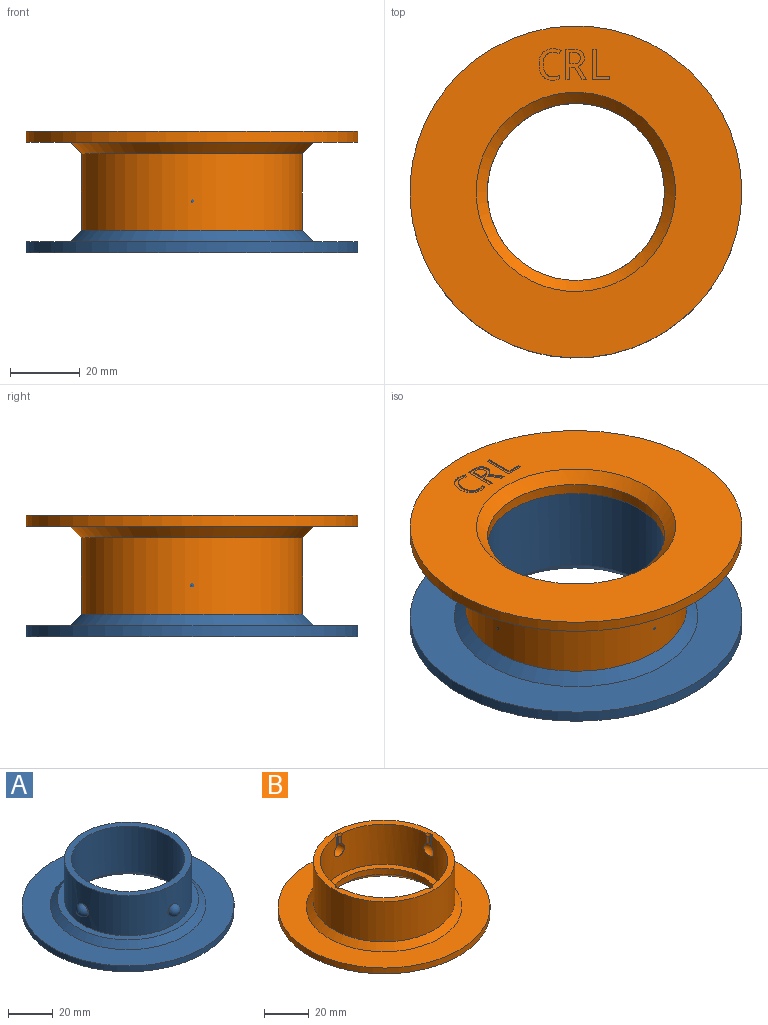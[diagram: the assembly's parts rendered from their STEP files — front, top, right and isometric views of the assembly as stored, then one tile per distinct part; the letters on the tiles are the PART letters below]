
ASSEMBLY  parts=2 mates=1
PART A: 62 faces, bbox 95.3x95.3x28.4 mm
  f0: plane 95.25x95.25mm, normal (0,0,-1), area 4479.2mm2, adj f10,f11,f27,f28,f29,f30,f31,f32
  f1: cylinder r=3.17mm len=6.35mm, axis (0,1,0), area 0.9mm2, adj f5,f20
  f2: cylinder r=3.17mm len=6.35mm, axis (0,1,0), area 0.9mm2, adj f5,f19
  f3: cylinder r=3.17mm len=6.35mm, axis (-1,0,0), area 0.9mm2, adj f5,f18
  f4: cylinder r=3.17mm len=6.35mm, axis (-1,0,0), area 0.9mm2, adj f5,f17
  f5: cylinder r=28.57mm len=57.15mm, axis (0,0,1), area 3833.8mm2, adj f1,f2,f3,f4,f8,f9,f13,f14
  f6: cylinder r=25.4mm len=50.8mm, axis (0,0,1), area 4027.3mm2, adj f9,f11
  f7: plane 95.25x95.25mm, normal (0,0,1), area 3293.6mm2, adj f10,f12
  f8: plane 63.5x63.5mm, normal (0,0,1), area 601.7mm2, adj f5,f12
  f9: plane 57.15x57.15mm, normal (0,0,1), area 538.4mm2, adj f5,f6
  f10: cylinder r=47.62mm len=95.25mm, axis (0,0,1), area 950.1mm2, adj f0,f7
  f11: cone r=28.57mm half-angle=45deg, axis (0,0,-1), area 761.4mm2, adj f0,f6
  f12: cone r=31.75mm half-angle=45deg, axis (0,0,-1), area 940.5mm2, adj f7,f8
  f13: cylinder r=3.17mm len=6.35mm, axis (0,1,0), area 0.9mm2, adj f5,f19
  f14: cylinder r=3.17mm len=6.35mm, axis (0,1,0), area 0.9mm2, adj f5,f20
  f15: cylinder r=3.17mm len=6.35mm, axis (-1,0,0), area 0.9mm2, adj f5,f17
  f16: cylinder r=3.17mm len=6.35mm, axis (-1,0,0), area 0.9mm2, adj f5,f18
  f17: sphere r=3.17mm, area 63.3mm2, adj f4,f15
  f18: sphere r=3.17mm, area 63.3mm2, adj f3,f16
  f19: sphere r=3.17mm, area 63.3mm2, adj f2,f13
  f20: sphere r=3.17mm, area 63.3mm2, adj f1,f14
  f21: plane 1.11x0.4mm, normal (0,1,0), area 0.4mm2, adj f22,f37,f38,f61
  f22: plane 3.65x0.4mm, normal (-1,0,0), area 1.4mm2, adj f21,f23,f38,f61
  f23: plane 1.07x0.4mm, normal (0,-1,0), area 0.4mm2, adj f22,f24,f38,f61
  f24: extruded ~1.74x0.42mm, area 0.7mm2, adj f23,f25,f38,f61
  f25: extruded ~1.37x0.54mm, area 0.6mm2, adj f24,f26,f38,f61
  f26: extruded ~1.42x0.55mm, area 0.6mm2, adj f25,f37,f38,f61
  f27: plane 4.08x0.4mm, normal (-1,0,0), area 1.6mm2, adj f0,f28,f36,f38
  f28: plane 1.54x0.4mm, normal (0,-1,0), area 0.6mm2, adj f0,f27,f29,f38
  f29: plane 4.08x2.36mm, normal (0.87,-0.5,0), area 1.9mm2, adj f0,f28,f30,f38
  f30: plane 1.48x0.4mm, normal (0,-1,0), area 0.6mm2, adj f0,f29,f31,f38
  f31: plane 4.42x2.68mm, normal (-0.86,0.52,0), area 2.1mm2, adj f0,f30,f32,f38
  f32: extruded ~2.65x1.95mm, area 1.4mm2, adj f0,f31,f33,f38
  f33: extruded ~3.51x2.8mm, area 2mm2, adj f0,f32,f34,f38
  f34: plane 2.41x0.4mm, normal (0,1,0), area 1mm2, adj f0,f33,f35,f38
  f35: plane 9.87x0.4mm, normal (1,0,0), area 3.9mm2, adj f0,f34,f36,f38
  f36: plane 1.26x0.4mm, normal (0,-1,0), area 0.5mm2, adj f0,f27,f35,f38
  f37: extruded ~1.7x0.45mm, area 0.7mm2, adj f21,f26,f38,f61
  f38: plane 9.87x6.65mm, normal (0,0,-1), area 30.7mm2, adj f21,f22,f23,f24,f25,f26,f27,f28
  f39: plane 9.87x0.4mm, normal (1,0,0), area 3.9mm2, adj f0,f40,f44,f45
  f40: plane 5.55x0.4mm, normal (0,-1,0), area 2.2mm2, adj f0,f39,f41,f45
  f41: plane 1.12x0.4mm, normal (-1,0,0), area 0.4mm2, adj f0,f40,f42,f45
  f42: plane 4.29x0.4mm, normal (0,1,0), area 1.7mm2, adj f0,f41,f43,f45
  f43: plane 8.75x0.4mm, normal (-1,0,0), area 3.5mm2, adj f0,f42,f44,f45
  f44: plane 1.26x0.4mm, normal (0,1,0), area 0.5mm2, adj f0,f39,f43,f45
  f45: plane 9.87x5.55mm, normal (0,0,-1), area 17.3mm2, adj f39,f40,f41,f42,f43,f44
  f46: plane 1.09x0.4mm, normal (-1,0,0), area 0.4mm2, adj f0,f47,f59,f60
  f47: extruded ~2.21x0.4mm, area 0.9mm2, adj f0,f46,f48,f60
  f48: extruded ~2.37x1.02mm, area 1.1mm2, adj f0,f47,f49,f60
  f49: extruded ~2.95x0.81mm, area 1.2mm2, adj f0,f48,f50,f60
  f50: extruded ~2.9x0.86mm, area 1.2mm2, adj f0,f49,f51,f60
  f51: extruded ~2.32x1.07mm, area 1mm2, adj f0,f50,f52,f60
  f52: extruded ~2.06x0.53mm, area 0.9mm2, adj f0,f51,f53,f60
  f53: plane 1.05x0.53mm, normal (-0.89,-0.45,0), area 0.5mm2, adj f0,f52,f54,f60
  f54: extruded ~2.59x0.58mm, area 1.1mm2, adj f0,f53,f55,f60
  f55: extruded ~3.3x1.36mm, area 1.5mm2, adj f0,f54,f56,f60
  f56: extruded ~3.7x1.21mm, area 1.6mm2, adj f0,f55,f57,f60
  f57: extruded ~3.76x1.11mm, area 1.6mm2, adj f0,f56,f58,f60
  f58: extruded ~3.19x1.32mm, area 1.4mm2, adj f0,f57,f59,f60
  f59: extruded ~2.42x0.4mm, area 1mm2, adj f0,f46,f58,f60
  f60: plane 10.15x7.1mm, normal (0,0,-1), area 22.2mm2, adj f46,f47,f48,f49,f50,f51,f52,f53
  f61: plane 3.65x3.36mm, normal (0,0,-1), area 11mm2, adj f21,f22,f23,f24,f25,f26,f37
PART B: 79 faces, bbox 95.3x95.3x28.4 mm
  f0: plane 95.25x95.25mm, normal (0,0,-1), area 4496.2mm2, adj f10,f12,f44,f45,f46,f47,f48,f49
  f1: plane 63.5x63.5mm, normal (0,0,1), area 587.1mm2, adj f2,f7,f26,f27,f28,f29,f30,f31
  f2: cylinder r=28.57mm len=57.15mm, axis (0,0,1), area 3764.1mm2, adj f1,f3,f4,f5,f6,f8,f18,f19
  f3: sphere r=3.17mm, area 55.2mm2, adj f2,f17,f22,f23
  f4: sphere r=3.17mm, area 55.2mm2, adj f2,f16,f18,f19
  f5: sphere r=3.17mm, area 55.2mm2, adj f2,f15,f20,f21
  f6: sphere r=3.17mm, area 55.2mm2, adj f2,f14,f24,f25
  f7: cylinder r=31.75mm len=63.5mm, axis (0,0,1), area 4400.8mm2, adj f1,f13
  f8: plane 57.15x57.15mm, normal (0,0,1), area 538.4mm2, adj f2,f9
  f9: cylinder r=25.4mm len=50.8mm, axis (0,0,1), area 506.7mm2, adj f8,f12
  f10: cylinder r=47.62mm len=95.25mm, axis (0,0,1), area 950.1mm2, adj f0,f11
  f11: plane 95.25x95.25mm, normal (0,0,1), area 3293.6mm2, adj f10,f13
  f12: cone r=28.57mm half-angle=45deg, axis (0,0,-1), area 761.4mm2, adj f0,f9
  f13: cone r=31.75mm half-angle=45deg, axis (0,0,-1), area 940.5mm2, adj f7,f11
  f14: plane 3.96x0.38mm, normal (1,0,0), area 1.5mm2, adj f6,f24,f25,f27
  f15: plane 3.96x0.38mm, normal (-1,0,0), area 1.5mm2, adj f5,f20,f21,f33
  f16: plane 3.96x0.38mm, normal (0,-1,0), area 1.5mm2, adj f4,f18,f19,f30
  f17: plane 3.96x0.38mm, normal (0,1,0), area 1.5mm2, adj f3,f22,f23,f36
  f18: cylinder r=1.59mm len=4.17mm, axis (0,0,1), area 7mm2, adj f2,f4,f16,f29
  f19: cylinder r=1.59mm len=4.17mm, axis (0,0,1), area 7mm2, adj f2,f4,f16,f31
  f20: cylinder r=1.59mm len=4.17mm, axis (0,0,1), area 7mm2, adj f2,f5,f15,f32
  f21: cylinder r=1.59mm len=4.17mm, axis (0,0,1), area 7mm2, adj f2,f5,f15,f34
  f22: cylinder r=1.59mm len=4.17mm, axis (0,0,1), area 7mm2, adj f2,f3,f17,f37
  f23: cylinder r=1.59mm len=4.17mm, axis (0,0,1), area 7mm2, adj f2,f3,f17,f35
  f24: cylinder r=1.59mm len=4.17mm, axis (0,0,1), area 7mm2, adj f2,f6,f14,f28
  f25: cylinder r=1.59mm len=4.17mm, axis (0,0,1), area 7mm2, adj f2,f6,f14,f26
  f26: cone r=1.98mm half-angle=15deg, axis (0,0,1), area 3.1mm2, adj f1,f2,f25,f27
  f27: plane 1.48x0.4mm, normal (0.97,0,0.26), area 0.6mm2, adj f1,f14,f26,f28
  f28: cone r=1.98mm half-angle=15deg, axis (0,0,1), area 3.1mm2, adj f1,f2,f24,f27
  f29: cone r=1.98mm half-angle=15deg, axis (0,0,1), area 3.1mm2, adj f1,f2,f18,f30
  f30: plane 1.48x0.4mm, normal (0,-0.97,0.26), area 0.6mm2, adj f1,f16,f29,f31
  f31: cone r=1.98mm half-angle=15deg, axis (0,0,1), area 3.1mm2, adj f1,f2,f19,f30
  f32: cone r=1.98mm half-angle=15deg, axis (0,0,1), area 3.1mm2, adj f1,f2,f20,f33
  f33: plane 1.48x0.4mm, normal (-0.97,0,0.26), area 0.6mm2, adj f1,f15,f32,f34
  f34: cone r=1.98mm half-angle=15deg, axis (0,0,1), area 3.1mm2, adj f1,f2,f21,f33
  f35: cone r=1.98mm half-angle=15deg, axis (0,0,1), area 3.1mm2, adj f1,f2,f23,f36
  f36: plane 1.48x0.4mm, normal (0,0.97,0.26), area 0.6mm2, adj f1,f17,f35,f37
  f37: cone r=1.98mm half-angle=15deg, axis (0,0,1), area 3.1mm2, adj f1,f2,f22,f36
  f38: plane 0.98x0.4mm, normal (0,1,0), area 0.4mm2, adj f39,f54,f55,f78
  f39: plane 3.25x0.4mm, normal (-1,0,0), area 1.3mm2, adj f38,f40,f55,f78
  f40: plane 0.95x0.4mm, normal (0,-1,0), area 0.4mm2, adj f39,f41,f55,f78
  f41: extruded ~1.55x0.4mm, area 0.6mm2, adj f40,f42,f55,f78
  f42: extruded ~1.22x0.48mm, area 0.5mm2, adj f41,f43,f55,f78
  f43: extruded ~1.26x0.49mm, area 0.6mm2, adj f42,f54,f55,f78
  f44: plane 3.63x0.4mm, normal (-1,0,0), area 1.4mm2, adj f0,f45,f53,f55
  f45: plane 1.37x0.4mm, normal (0,-1,0), area 0.5mm2, adj f0,f44,f46,f55
  f46: plane 3.63x2.1mm, normal (0.87,-0.5,0), area 1.7mm2, adj f0,f45,f47,f55
  f47: plane 1.31x0.4mm, normal (0,-1,0), area 0.5mm2, adj f0,f46,f48,f55
  f48: plane 3.93x2.38mm, normal (-0.86,0.52,0), area 1.8mm2, adj f0,f47,f49,f55
  f49: extruded ~2.35x1.73mm, area 1.2mm2, adj f0,f48,f50,f55
  f50: extruded ~3.12x2.49mm, area 1.8mm2, adj f0,f49,f51,f55
  f51: plane 2.14x0.4mm, normal (0,1,0), area 0.9mm2, adj f0,f50,f52,f55
  f52: plane 8.77x0.4mm, normal (1,0,0), area 3.5mm2, adj f0,f51,f53,f55
  f53: plane 1.12x0.4mm, normal (0,-1,0), area 0.4mm2, adj f0,f44,f52,f55
  f54: extruded ~1.51x0.4mm, area 0.6mm2, adj f38,f43,f55,f78
  f55: plane 8.77x5.91mm, normal (0,0,-1), area 24.3mm2, adj f38,f39,f40,f41,f42,f43,f44,f45
  f56: plane 0.97x0.4mm, normal (-1,0,0), area 0.4mm2, adj f0,f57,f69,f70
  f57: extruded ~1.96x0.4mm, area 0.8mm2, adj f0,f56,f58,f70
  f58: extruded ~2.11x0.9mm, area 0.9mm2, adj f0,f57,f59,f70
  f59: extruded ~2.62x0.72mm, area 1.1mm2, adj f0,f58,f60,f70
  f60: extruded ~2.58x0.77mm, area 1.1mm2, adj f0,f59,f61,f70
  f61: extruded ~2.06x0.95mm, area 0.9mm2, adj f0,f60,f62,f70
  f62: extruded ~1.83x0.47mm, area 0.8mm2, adj f0,f61,f63,f70
  f63: plane 0.94x0.47mm, normal (-0.89,-0.45,0), area 0.4mm2, adj f0,f62,f64,f70
  f64: extruded ~2.3x0.51mm, area 0.9mm2, adj f0,f63,f65,f70
  f65: extruded ~2.94x1.21mm, area 1.3mm2, adj f0,f64,f66,f70
  f66: extruded ~3.29x1.07mm, area 1.4mm2, adj f0,f65,f67,f70
  f67: extruded ~3.34x0.98mm, area 1.4mm2, adj f0,f66,f68,f70
  f68: extruded ~2.84x1.18mm, area 1.3mm2, adj f0,f67,f69,f70
  f69: extruded ~2.15x0.4mm, area 0.9mm2, adj f0,f56,f68,f70
  f70: plane 9.02x6.31mm, normal (0,0,-1), area 17.5mm2, adj f56,f57,f58,f59,f60,f61,f62,f63
  f71: plane 8.77x0.4mm, normal (1,0,0), area 3.5mm2, adj f0,f72,f76,f77
  f72: plane 4.93x0.4mm, normal (0,-1,0), area 2mm2, adj f0,f71,f73,f77
  f73: plane 1x0.4mm, normal (-1,0,0), area 0.4mm2, adj f0,f72,f74,f77
  f74: plane 3.81x0.4mm, normal (0,1,0), area 1.5mm2, adj f0,f73,f75,f77
  f75: plane 7.78x0.4mm, normal (-1,0,0), area 3.1mm2, adj f0,f74,f76,f77
  f76: plane 1.12x0.4mm, normal (0,1,0), area 0.4mm2, adj f0,f71,f75,f77
  f77: plane 8.77x4.93mm, normal (0,0,-1), area 13.7mm2, adj f71,f72,f73,f74,f75,f76
  f78: plane 3.25x2.98mm, normal (0,0,-1), area 8.7mm2, adj f38,f39,f40,f41,f42,f43,f54
PLACE A rot(axis=(-0.03,-0.37,-0.93),0deg) t=(124.66,87.78,-34)mm
PLACE B rot(axis=(1,0,0),180deg) t=(124.66,87.78,-28.77)mm
MATE fastened B.f2 <-> A.f5  axis (0,0,-1) through (124.66,87.78,-42.38)mm
